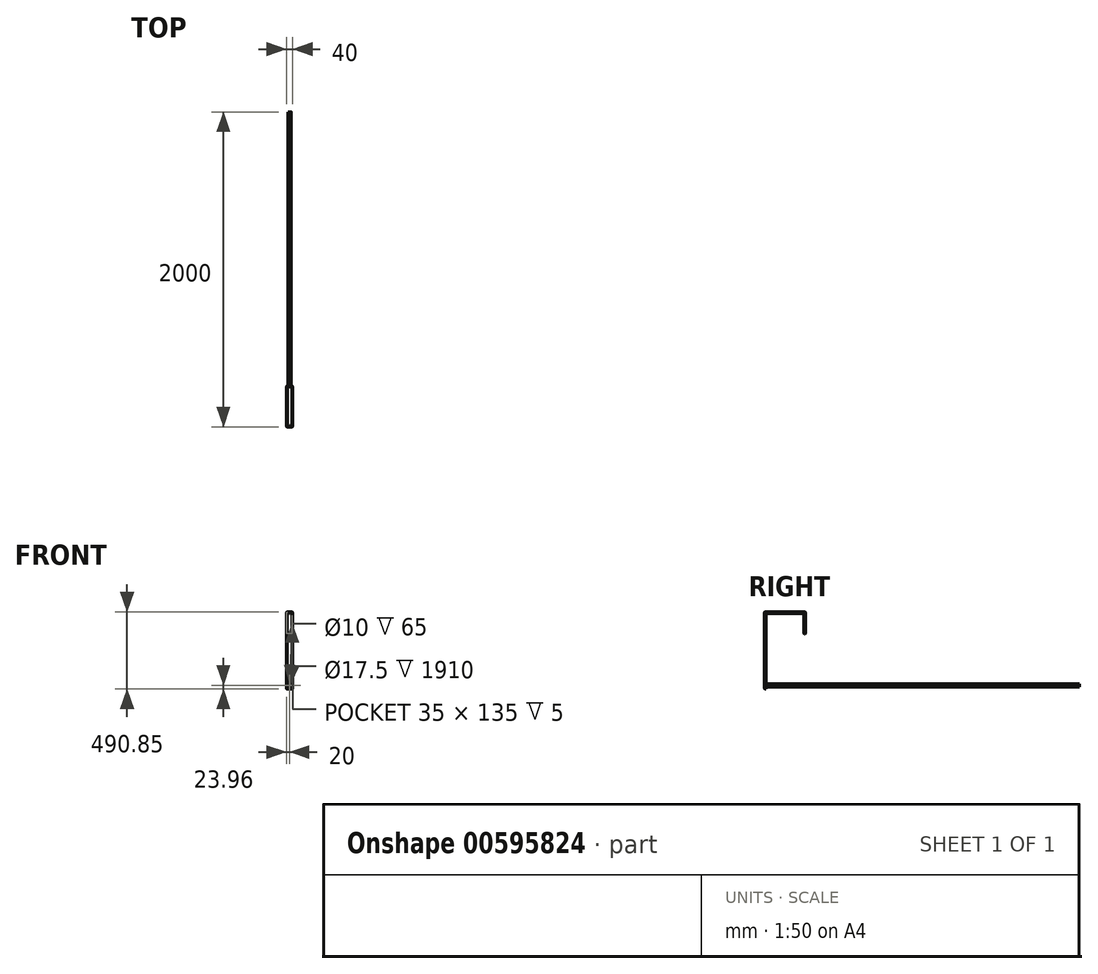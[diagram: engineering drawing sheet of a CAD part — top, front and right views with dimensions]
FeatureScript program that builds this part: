
annotation { "Feature Type Name" : "Feature", "Feature Type Description" : "" }
export const myFeature = defineFeature(function(context is Context, id is Id, definition is map)
    precondition{}
    {
        {
            var Q0;
            Q0=qCreatedBy(makeId("Front.planeOp"),FACE);
            var sketch = newSketch(context, id + "F0", { "sketchPlane" : qUnion([Q0])});
            skCircle(sketch, "E0", {"center": v(0, 0) * mm, "radius": 10 * mm});
            skSolve(sketch);
        }
        {
            var Q0;
            Q0=qCreatedBy(makeId("Front.planeOp"),FACE);
            var sketch = newSketch(context, id + "F1", { "sketchPlane" : qUnion([Q0])});
            skCircle(sketch, "E1", {"center": v(0, 0) * mm, "radius": 8.75 * mm});
            skSolve(sketch);
        }
        {
            var Q0;
            Q0=makeQuery(id+"F0.imprint","IMPRINT",FACE,{"disambiguationData":[TD([[makeQuery(id+"F0.imprint","IMPRINT",EDGE,{"derivedFrom":sQuery(id+"F0.wireOp",EDGE,"E0")}),1.0]])]});
            extrude(context, id + "F2", {"entities" : qUnion([Q0]), "oppositeDirection" : true, "depth" : 2000 * mm, "offsetDistance" : 25 * mm});
        }
        {
            var Q0;
            Q0=qSketchRegion(id+"F1",true);
            extrude(context, id + "F3", {"entities" : qUnion([Q0]), "operationType" : NewBodyOperationType.REMOVE, "oppositeDirection" : true, "depth" : 2000 * mm, "offsetDistance" : 25 * mm});
        }
        {
            var Q0;
            Q0=qCreatedBy(makeId("Right.planeOp"),FACE);
            cPlane(context, id + "F4", {"entities" : qUnion([Q0]), "cplaneType" : CPlaneType.OFFSET, "offset" : 20 * mm, "width" : 150 * mm, "height" : 150 * mm});
        }
        {
            var Q0;
            Q0=qCreatedBy(id+"F4.planeOp",FACE);
            var sketch = newSketch(context, id + "F5", { "sketchPlane" : qUnion([Q0])});
            skArc(sketch, "E2", {"start": v(0, -23.1) * mm, "mid": v(5, -23.96) * mm, "end": v(10, -23.1) * mm});
            skLineSegment(sketch, "E3", {"start": v(0, -23.1) * mm, "end": v(0, 466.9) * mm});
            skLineSegment(sketch, "E4", {"start": v(0, 466.9) * mm, "end": v(260, 466.9) * mm});
            skLineSegment(sketch, "E5", {"start": v(260, 466.9) * mm, "end": v(260, 326.9) * mm});
            skLineSegment(sketch, "E6", {"start": v(260, 326.9) * mm, "end": v(250, 326.9) * mm});
            skLineSegment(sketch, "E7", {"start": v(250, 326.9) * mm, "end": v(250, 456.9) * mm});
            skLineSegment(sketch, "E8", {"start": v(250, 456.9) * mm, "end": v(10, 456.9) * mm});
            skLineSegment(sketch, "E9", {"start": v(10, 456.9) * mm, "end": v(10, -23.1) * mm});
            skSolve(sketch);
        }
        {
            var Q0;
            Q0=qSketchRegion(id+"F5",true);
            extrude(context, id + "F6", {"entities" : qUnion([Q0]), "operationType" : NewBodyOperationType.ADD, "oppositeDirection" : true, "depth" : 40 * mm, "offsetDistance" : 25 * mm});
        }
        {
            var Q0;
            Q0=makeQuery(id+"F6.opExtrude","CAP_FACE",FACE,{"disambiguationData":[OSD([sQuery(id+"F5.wireOp",EDGE,"ZqaeSb9h-DRj7-tXTc-Ij0N-ZdABmIdTmdiv"),sQuery(id+"F5.wireOp",EDGE,"2cxdRBLy-XSOz-v9gC-QeX3-DMfJfcwrgfGG"),sQuery(id+"F5.wireOp",EDGE,"HlKo1tSY-Q5QG-WWil-dwIK-WjqPjtTRjNrt"),sQuery(id+"F5.wireOp",EDGE,"284f362e-461d-4ea2-9a0a-4d998c6a0b75")])],"isStart":true});
            var Q1;
            Q1=makeQuery(id+"F2.opExtrude","SWEPT_BODY",BODY,{"disambiguationData":[OSD([sQuery(id+"F0.wireOp",EDGE,"E0")])]});
            shell(context, id + "F7", {"isHollow" : true, "entities" : qUnion([Q0]), "parts" : qUnion([Q1]), "thickness" : 2.5 * mm});
        }
        {
            var Q0;
            Q0=makeQuery(id+"F6.opExtrude","SWEPT_FACE",FACE,{"disambiguationData":[OSD([sQuery(id+"F5.wireOp",EDGE,"E5")])]});
            var Q1;
            Q1=makeQuery(id+"F6.opExtrude","SWEPT_FACE",FACE,{"disambiguationData":[OSD([sQuery(id+"F5.wireOp",EDGE,"E4")])]});
            var Q2;
            {var subQ0=sQuery(id+"F5.wireOp",EDGE,"E9");Q2=makeQuery(id+"F6.boolean.opBoolean","SPLIT",FACE,{"disambiguationData":[TD([makeQuery(id+"F2.opExtrude","SWEPT_FACE",FACE,{"disambiguationData":[OSD([sQuery(id+"F0.wireOp",EDGE,"E0")])]})])],"derivedFrom":makeQuery(id+"F6.opExtrude","SWEPT_FACE",FACE,{"disambiguationData":[OSD([subQ0])]})});}
            var Q3;
            Q3=makeQuery(id+"F6.opExtrude","CAP_EDGE",EDGE,{"disambiguationData":[OSD([sQuery(id+"F5.wireOp",EDGE,"E3")])],"isStart":false});
            var Q4;
            Q4=makeQuery(id+"F6.opExtrude","CAP_EDGE",EDGE,{"disambiguationData":[OSD([sQuery(id+"F5.wireOp",EDGE,"E8")])],"isStart":false});
            var Q5;
            Q5=makeQuery(id+"F6.opExtrude","CAP_EDGE",EDGE,{"disambiguationData":[OSD([sQuery(id+"F5.wireOp",EDGE,"E6")])],"isStart":false});
            var Q6;
            Q6=makeQuery(id+"F6.opExtrude","CAP_EDGE",EDGE,{"disambiguationData":[OSD([sQuery(id+"F5.wireOp",EDGE,"E7")])],"isStart":true});
            var Q7;
            Q7=makeQuery(id+"F6.opExtrude","SWEPT_EDGE",EDGE,{"disambiguationData":[OSD([sQuery(id+"F5.wireOp",EDGE,"E6"),sQuery(id+"F5.wireOp",EDGE,"E7")])]});
            var Q8;
            Q8=makeQuery(id+"F6.opExtrude","CAP_EDGE",EDGE,{"disambiguationData":[OSD([sQuery(id+"F5.wireOp",EDGE,"E7")])],"isStart":false});
            var Q9;
            Q9=makeQuery(id+"F6.opExtrude","CAP_EDGE",EDGE,{"disambiguationData":[OSD([sQuery(id+"F5.wireOp",EDGE,"E3")])],"isStart":true});
            var Q10;
            Q10=makeQuery(id+"F6.opExtrude","SWEPT_EDGE",EDGE,{"disambiguationData":[OSD([sQuery(id+"F5.wireOp",EDGE,"E2"),sQuery(id+"F5.wireOp",EDGE,"E3")])]});
            var Q11;
            Q11=makeQuery(id+"F6.opExtrude","CAP_EDGE",EDGE,{"disambiguationData":[OSD([sQuery(id+"F5.wireOp",EDGE,"E2")])],"isStart":true});
            var Q12;
            Q12=makeQuery(id+"F6.opExtrude","CAP_EDGE",EDGE,{"disambiguationData":[OSD([sQuery(id+"F5.wireOp",EDGE,"E2")])],"isStart":false});
            chamfer(context, id + "F8", {"entities" : qUnion([Q0, Q1, Q2, Q3, Q4, Q5, Q6, Q7, Q8, Q9, Q10, Q11, Q12]), "width" : 3 * mm, "tangentPropagation" : true});
        }
        {
            var Q0;
            Q0=qCreatedBy(makeId("Front.planeOp"),FACE);
            cPlane(context, id + "F9", {"entities" : qUnion([Q0]), "cplaneType" : CPlaneType.OFFSET, "offset" : (2000 - 80) * mm, "oppositeDirection" : true, "width" : 150 * mm, "height" : 150 * mm});
        }
        {
            var Q0;
            Q0=qCreatedBy(id+"F9.planeOp",FACE);
            var sketch = newSketch(context, id + "F10", { "sketchPlane" : qUnion([Q0])});
            skCircle(sketch, "E10", {"center": v(0, 0) * mm, "radius": 10.1 * mm});
            skSolve(sketch);
        }
        {
            var Q0;
            Q0 = qSketchRegion(id + "F10", true);
            extrude(context, id + "F11", {"entities" : qUnion([Q0]), "operationType" : NewBodyOperationType.ADD, "oppositeDirection" : true, "depth" : 80 * mm, "offsetDistance" : 25 * mm});
        }
        {
            var Q0;
            Q0=qCreatedBy(id+"F9.planeOp",FACE);
            cPlane(context, id + "F12", {"entities" : qUnion([Q0]), "cplaneType" : CPlaneType.OFFSET, "offset" : 80 * mm, "oppositeDirection" : true, "width" : 150 * mm, "height" : 150 * mm});
        }
        {
            var Q0;
            Q0=qCreatedBy(id+"F12.planeOp",FACE);
            var sketch = newSketch(context, id + "F13", { "sketchPlane" : qUnion([Q0])});
            skCircle(sketch, "E11", {"center": v(0, 0) * mm, "radius": 5 * mm});
            skSolve(sketch);
        }
        {
            var Q0;
            Q0 = qSketchRegion(id + "F13", true);
            var Q1;
            Q1 = qConstructionFilter(qBodyType(qCreatedBy(id + "F13" ,EDGE), BodyType.WIRE), ConstructionObject.NO);
            extrude(context, id + "F14", {"entities" : qUnion([Q0]), "operationType" : NewBodyOperationType.REMOVE, "surfaceEntities" : qUnion([Q1]), "depth" : 65 * mm, "offsetDistance" : 25 * mm});
        }
    });
